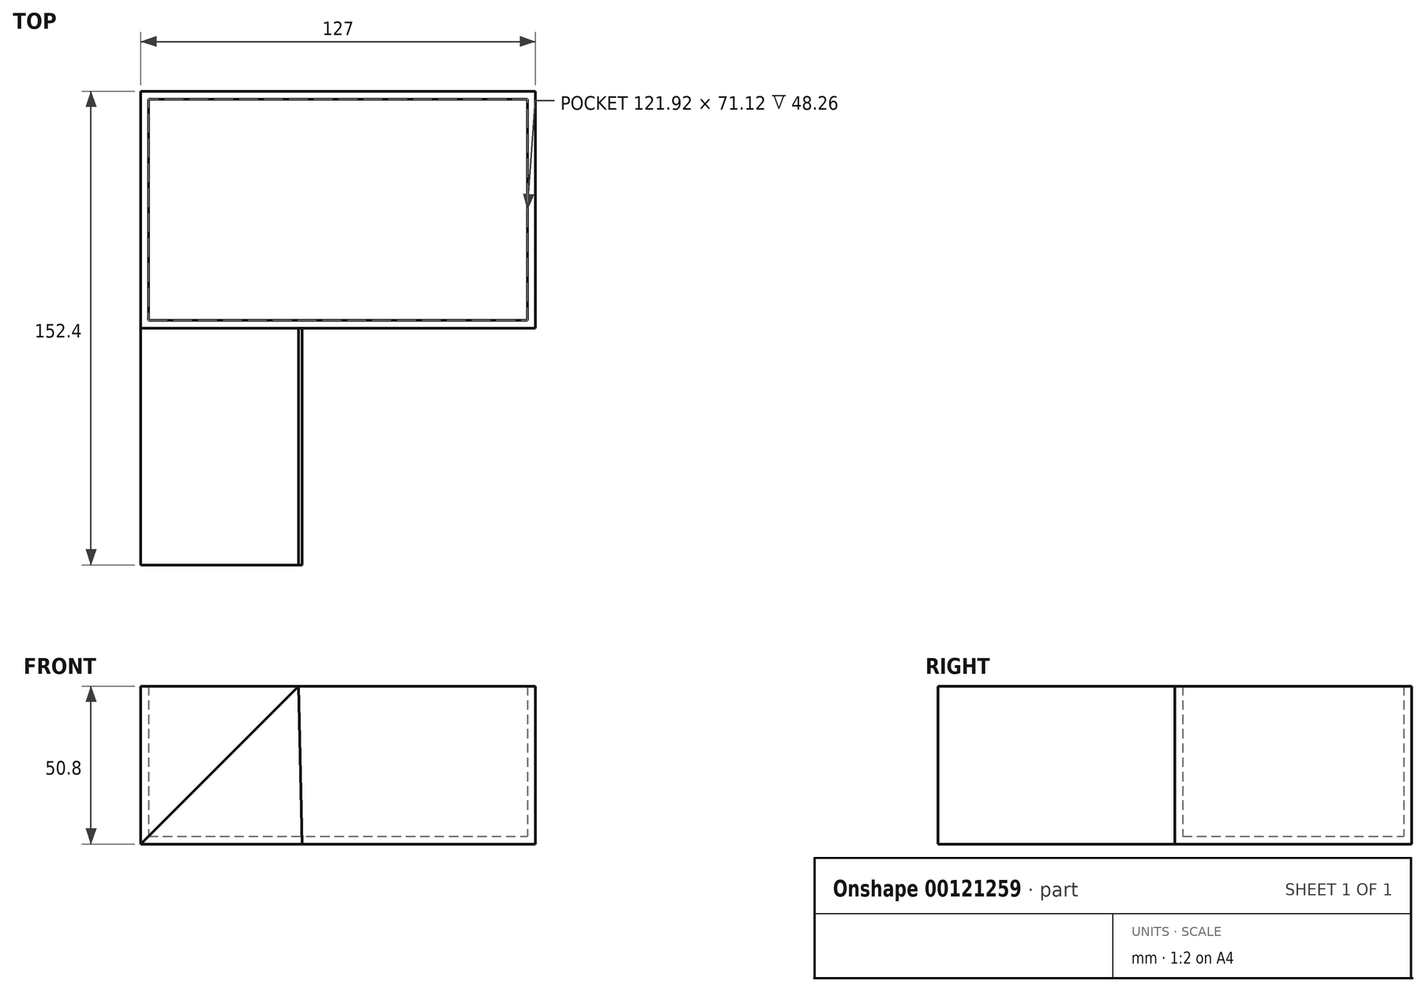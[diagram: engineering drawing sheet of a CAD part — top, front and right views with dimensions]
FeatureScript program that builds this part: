
annotation { "Feature Type Name" : "Feature", "Feature Type Description" : "" }
export const myFeature = defineFeature(function(context is Context, id is Id, definition is map)
    precondition{}
    {
        {
            var Q0;
            Q0=qCreatedBy(makeId("Top.planeOp"),FACE);
            var sketch = newSketch(context, id + "F0", { "sketchPlane" : qUnion([Q0])});
            skLineSegment(sketch, "E0.bottom", {"start": v(0, 0) * mm, "end": v(127, 0) * mm});
            skLineSegment(sketch, "E0.top", {"start": v(0, 76.2) * mm, "end": v(127, 76.2) * mm});
            skLineSegment(sketch, "E0.left", {"start": v(0, 0) * mm, "end": v(0, 76.2) * mm});
            skLineSegment(sketch, "E0.right", {"start": v(127, 0) * mm, "end": v(127, 76.2) * mm});
            skSolve(sketch);
        }
        {
            var Q0;
            Q0 = qSketchRegion(id + "F0", true);
            extrude(context, id + "F1", {"entities" : qUnion([Q0]), "depth" : 50.8 * mm});
        }
        {
            var Q0;
            Q0=makeQuery(id+"F1.opExtrude","CAP_FACE",FACE,{"disambiguationData":[OSD([sQuery(id+"F0.wireOp",EDGE,"E0.bottom"),sQuery(id+"F0.wireOp",EDGE,"E0.top"),sQuery(id+"F0.wireOp",EDGE,"E0.left"),sQuery(id+"F0.wireOp",EDGE,"E0.right")])],"isStart":false});
            shell(context, id + "F2", {"entities" : qUnion([Q0]), "thickness" : 2.54 * mm});
        }
        {
            var Q0;
            Q0=makeQuery(id+"F1.opExtrude","SWEPT_FACE",FACE,{"disambiguationData":[OSD([sQuery(id+"F0.wireOp",EDGE,"E0.bottom")])]});
            var sketch = newSketch(context, id + "F3", { "sketchPlane" : qUnion([Q0])});
            skLineSegment(sketch, "E1", {"start": v(0, 0) * mm, "end": v(50.8, 50.8) * mm});
            skLineSegment(sketch, "E2", {"start": v(50.8, 50.8) * mm, "end": v(51.9, 0) * mm});
            skLineSegment(sketch, "E3", {"start": v(51.9, 0) * mm, "end": v(0, 0) * mm});
            skSolve(sketch);
        }
        {
            var Q0;
            Q0 = qSketchRegion(id + "F3", true);
            extrude(context, id + "F4", {"entities" : qUnion([Q0]), "operationType" : NewBodyOperationType.ADD, "depth" : 76.2 * mm});
        }
    });
